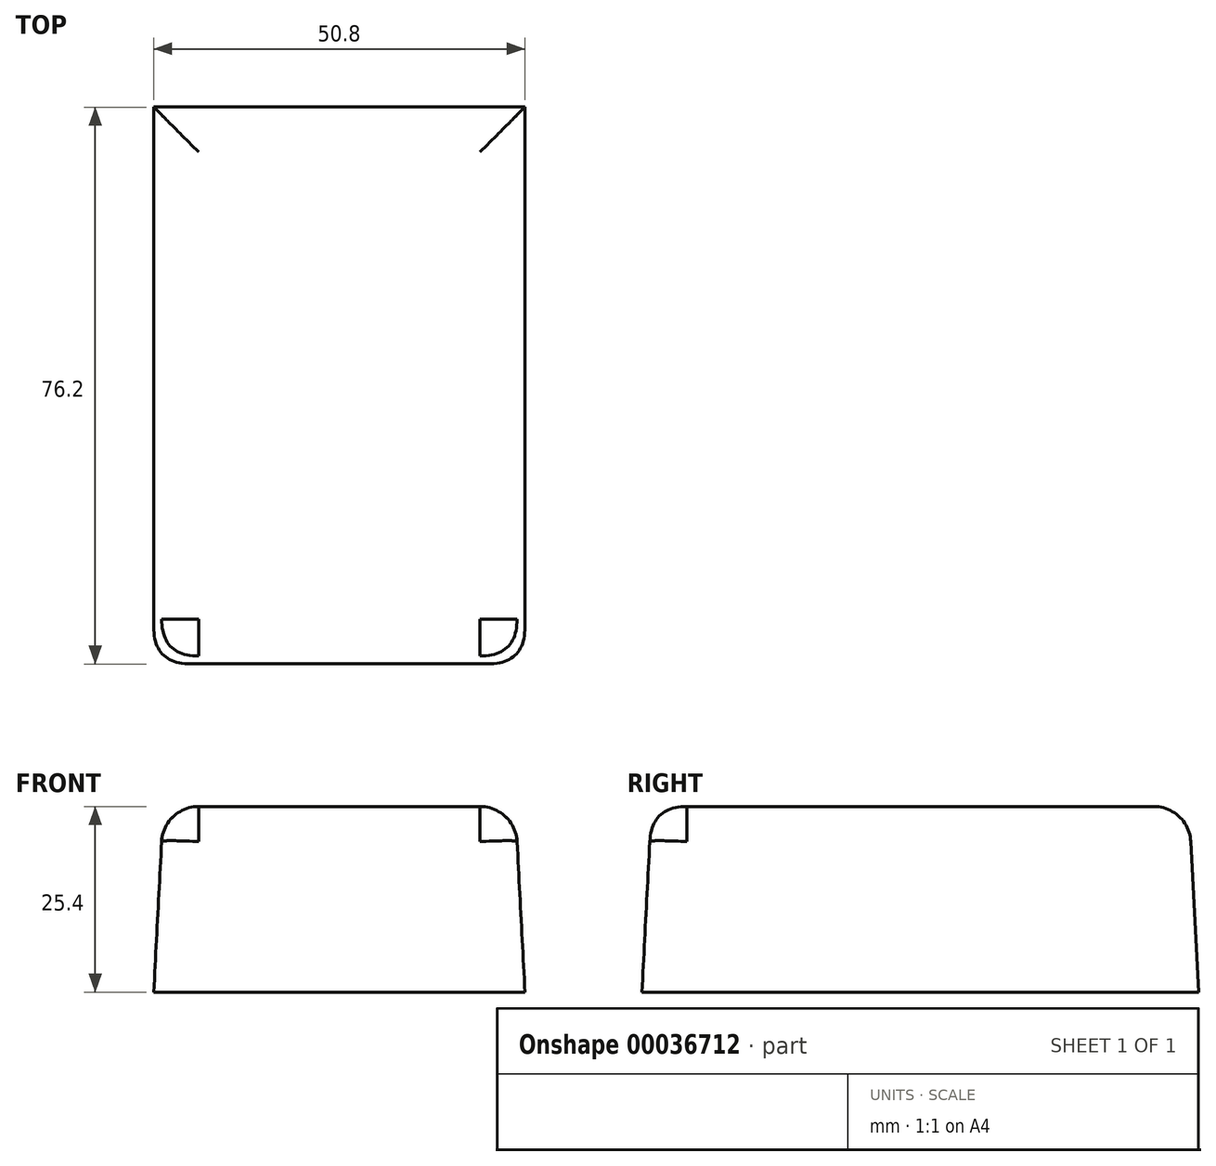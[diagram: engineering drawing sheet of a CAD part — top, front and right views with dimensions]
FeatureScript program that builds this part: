
annotation { "Feature Type Name" : "Feature", "Feature Type Description" : "" }
export const myFeature = defineFeature(function(context is Context, id is Id, definition is map)
    precondition{}
    {
        {
            var Q0;
            Q0=qCreatedBy(makeId("Top.planeOp"),FACE);
            var sketch = newSketch(context, id + "F0", { "sketchPlane" : qUnion([Q0])});
            skLineSegment(sketch, "E0.bottom", {"start": v(-50.8, -45.14) * mm, "end": v(0, -45.14) * mm});
            skLineSegment(sketch, "E0.top", {"start": v(-50.8, 31.06) * mm, "end": v(0, 31.06) * mm});
            skLineSegment(sketch, "E0.left", {"start": v(-50.8, -45.14) * mm, "end": v(-50.8, 31.06) * mm});
            skLineSegment(sketch, "E0.right", {"start": v(0, -45.14) * mm, "end": v(0, 31.06) * mm});
            skSolve(sketch);
        }
        {
            var Q0;
            Q0 = qSketchRegion(id + "F0", true);
            var Q1;
            Q1=makeQuery(id+"F0.imprint","IMPRINT",FACE,{"disambiguationData":[TD([[makeQuery(id+"F0.imprint","IMPRINT",EDGE,{"derivedFrom":sQuery(id+"F0.wireOp",EDGE,"E0.bottom")}),1.0]])]});
            extrude(context, id + "F1", {"entities" : qUnion([Q0, Q1]), "depth" : 25.4 * mm, "hasDraft" : true, "draftAngle" : 3 * degree, "draftPullDirection" : true});
        }
        {
            var Q0;
            Q0=makeQuery(id+"F1.opExtrude","CAP_EDGE",EDGE,{"disambiguationData":[OSD([sQuery(id+"F0.wireOp",EDGE,"E0.left")])],"isStart":false});
            var Q1;
            Q1=makeQuery(id+"F1.opExtrude","CAP_EDGE",EDGE,{"disambiguationData":[OSD([sQuery(id+"F0.wireOp",EDGE,"E0.top")])],"isStart":false});
            var Q2;
            Q2=makeQuery(id+"F1.opExtrude","CAP_EDGE",EDGE,{"disambiguationData":[OSD([sQuery(id+"F0.wireOp",EDGE,"E0.right")])],"isStart":false});
            fillet(context, id + "F2", {"entities" : qUnion([Q0, Q1, Q2]), "radius" : 5.08 * mm, "tangentPropagation" : true, "allowEdgeOverflow" : false});
        }
        {
            var Q0;
            Q0=makeQuery(id+"F1.opExtrude","CAP_EDGE",EDGE,{"disambiguationData":[OSD([sQuery(id+"F0.wireOp",EDGE,"E0.bottom")])],"isStart":false});
            fillet(context, id + "F3", {"entities" : qUnion([Q0]), "radius" : 5.08 * mm, "tangentPropagation" : true, "rho" : 0.5, "crossSection" : FilletCrossSection.CONIC, "allowEdgeOverflow" : false});
        }
    });
